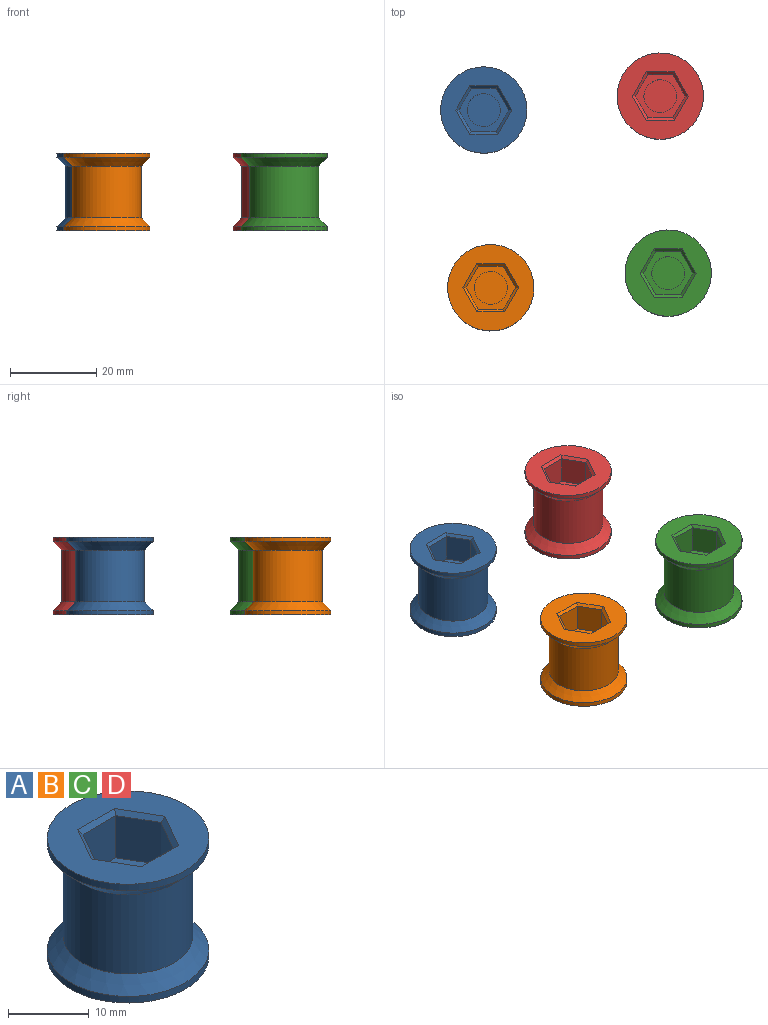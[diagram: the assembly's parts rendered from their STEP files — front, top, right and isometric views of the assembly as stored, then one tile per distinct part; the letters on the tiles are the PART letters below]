
ASSEMBLY  parts=4 mates=3
PART A: 22 faces, bbox 20x20x18 mm
  f0: cylinder r=3.8mm len=8mm, axis (0,0,-1), area 191mm2, adj f1,f2
  f1: plane 11.55x10mm, normal (0,0,1), area 41.2mm2, adj f0,f3,f4,f5,f6,f7,f8
  f2: plane 7.6x7.6mm, normal (0,0,1), area 45.4mm2, adj f0
  f3: plane 6.4x5mm, normal (0.87,0.5,0), area 37mm2, adj f1,f4,f8,f13
  f4: plane 6.4x5.77mm, normal (0,1,0), area 37mm2, adj f1,f3,f5,f15
  f5: plane 6.4x5mm, normal (-0.87,0.5,0), area 37mm2, adj f1,f4,f6,f14
  f6: plane 6.4x5mm, normal (-0.87,-0.5,0), area 37mm2, adj f1,f5,f7,f12
  f7: plane 6.4x5.77mm, normal (0,-1,0), area 37mm2, adj f1,f6,f8,f10
  f8: plane 6.4x5mm, normal (0.87,-0.5,0), area 37mm2, adj f1,f3,f7,f11
  f9: plane 20x20mm, normal (0,0,1), area 205.5mm2, adj f10,f11,f12,f13,f14,f15,f16
  f10: plane 6.47x0.6mm, normal (0,-0.71,0.71), area 5.2mm2, adj f7,f9,f11,f12
  f11: plane 5.6x3.58mm, normal (0.61,-0.35,0.71), area 5.2mm2, adj f8,f9,f10,f13
  f12: plane 5.6x3.58mm, normal (-0.61,-0.35,0.71), area 5.2mm2, adj f6,f9,f10,f14
  f13: plane 5.6x3.58mm, normal (0.61,0.35,0.71), area 5.2mm2, adj f3,f9,f11,f15
  f14: plane 5.6x3.58mm, normal (-0.61,0.35,0.71), area 5.2mm2, adj f5,f9,f12,f15
  f15: plane 6.47x0.6mm, normal (0,0.71,0.71), area 5.2mm2, adj f4,f9,f13,f14
  f16: cylinder r=10mm len=20mm, axis (0,0,1), area 62.8mm2, adj f9,f21
  f17: plane 20x20mm, normal (0,0,-1), area 314.2mm2, adj f18
  f18: cylinder r=10mm len=20mm, axis (0,0,1), area 62.8mm2, adj f17,f20
  f19: cylinder r=8mm len=16mm, axis (0,0,-1), area 603.2mm2, adj f20,f21
  f20: cone r=8mm half-angle=45deg, axis (0,0,-1), area 159.9mm2, adj f18,f19
  f21: cone r=10mm half-angle=45deg, axis (0,0,1), area 159.9mm2, adj f16,f19
PART B: same geometry as A
PART C: same geometry as A
PART D: same geometry as A
PLACE A t=(-21.34,20.04,-15.78)mm
PLACE B t=(-19.72,-21.15,-15.78)mm
PLACE C t=(21.38,-17.76,-15.78)mm
PLACE D t=(19.56,23.25,-15.78)mm
MATE planar A.f16 <-> B.f16  axis (0,0,-1) through (-21.34,20.04,-18.78)mm
MATE planar D.f16 <-> A.f16  axis (0,0,-1) through (19.56,23.25,-18.78)mm
MATE planar D.f16 <-> C.f16  axis (0,0,-1) through (19.56,23.25,-18.78)mm
